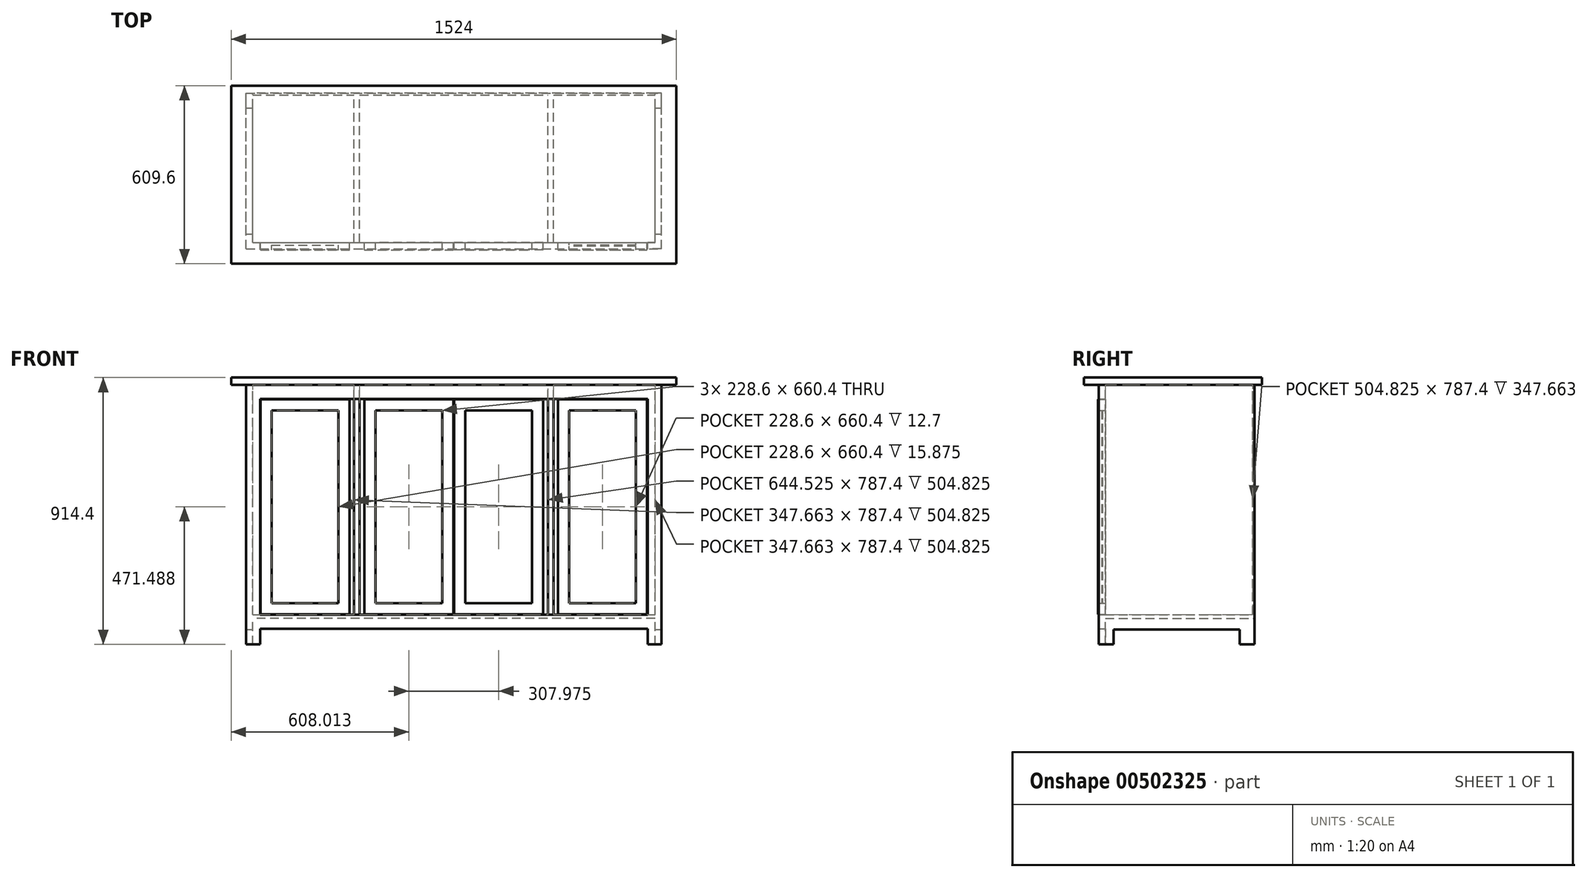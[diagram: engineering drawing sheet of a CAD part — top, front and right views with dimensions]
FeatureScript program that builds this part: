
annotation { "Feature Type Name" : "Feature", "Feature Type Description" : "" }
export const myFeature = defineFeature(function(context is Context, id is Id, definition is map)
    precondition{}
    {
        {
            var Q0;
            Q0=qCreatedBy(makeId("Top.planeOp"),FACE);
            var sketch = newSketch(context, id + "F0", { "sketchPlane" : qUnion([Q0])});
            skLineSegment(sketch, "E0.bottom", {"start": v(762, 304.8) * mm, "end": v(-762, 304.8) * mm});
            skLineSegment(sketch, "E0.top", {"start": v(762, -304.8) * mm, "end": v(-762, -304.8) * mm});
            skLineSegment(sketch, "E0.left", {"start": v(762, 304.8) * mm, "end": v(762, -304.8) * mm});
            skLineSegment(sketch, "E0.right", {"start": v(-762, 304.8) * mm, "end": v(-762, -304.8) * mm});
            skPoint(sketch, "E0.middle", {"position": v(0, 0) * mm});
            skSolve(sketch);
        }
        {
            var Q0;
            Q0=makeQuery(id+"F0.imprint","IMPRINT",FACE,{"disambiguationData":[TD([[makeQuery(id+"F0.imprint","IMPRINT",EDGE,{"derivedFrom":sQuery(id+"F0.wireOp",EDGE,"E0.bottom")}),1.0]])]});
            extrude(context, id + "F1", {"entities" : qUnion([Q0]), "depth" : 25.4 * mm});
        }
        {
            var Q0;
            Q0=makeQuery(id+"F1.opExtrude","CAP_FACE",FACE,{"disambiguationData":[OSD([sQuery(id+"F0.wireOp",EDGE,"E0.bottom"),sQuery(id+"F0.wireOp",EDGE,"E0.top"),sQuery(id+"F0.wireOp",EDGE,"E0.left"),sQuery(id+"F0.wireOp",EDGE,"E0.right")])],"isStart":true});
            var sketch = newSketch(context, id + "F2", { "sketchPlane" : qUnion([Q0])});
            skLineSegment(sketch, "E1.bottom", {"start": v(-711.2, 254) * mm, "end": v(711.2, 254) * mm, "construction": true});
            skLineSegment(sketch, "E1.top", {"start": v(-711.2, -279.4) * mm, "end": v(711.2, -279.4) * mm, "construction": true});
            skLineSegment(sketch, "E1.left", {"start": v(-711.2, 254) * mm, "end": v(-711.2, -279.4) * mm, "construction": true});
            skLineSegment(sketch, "E1.right", {"start": v(711.2, 254) * mm, "end": v(711.2, -279.4) * mm, "construction": true});
            skPoint(sketch, "E1.middle", {"position": v(0, -12.7) * mm});
            skLineSegment(sketch, "E2.bottom", {"start": v(-711.2, 254) * mm, "end": v(-688.98, 254) * mm, "construction": true});
            skLineSegment(sketch, "E2.top", {"start": v(-711.2, 231.78) * mm, "end": v(-688.98, 231.78) * mm, "construction": true});
            skLineSegment(sketch, "E2.left", {"start": v(-711.2, 254) * mm, "end": v(-711.2, 231.78) * mm, "construction": true});
            skLineSegment(sketch, "E2.right", {"start": v(-688.98, 254) * mm, "end": v(-688.98, 231.78) * mm, "construction": true});
            skLineSegment(sketch, "E3.bottom", {"start": v(-711.2, 231.78) * mm, "end": v(-688.98, 231.78) * mm});
            skLineSegment(sketch, "E3.top", {"start": v(-711.2, -279.4) * mm, "end": v(-688.98, -279.4) * mm});
            skLineSegment(sketch, "E3.left", {"start": v(-711.2, 231.78) * mm, "end": v(-711.2, -279.4) * mm});
            skLineSegment(sketch, "E3.right", {"start": v(-688.98, 231.78) * mm, "end": v(-688.98, -279.4) * mm});
            skLineSegment(sketch, "E4.MirrorCS", {"start": v(711.2, 231.78) * mm, "end": v(688.98, 231.78) * mm});
            skLineSegment(sketch, "E5.MirrorCS", {"start": v(711.2, 254) * mm, "end": v(711.2, 231.78) * mm, "construction": true});
            skLineSegment(sketch, "E6.MirrorCS", {"start": v(711.2, 231.78) * mm, "end": v(688.98, 231.78) * mm, "construction": true});
            skLineSegment(sketch, "E7.MirrorCS", {"start": v(688.98, 254) * mm, "end": v(688.98, 231.78) * mm, "construction": true});
            skLineSegment(sketch, "E8.MirrorCS", {"start": v(711.2, 254) * mm, "end": v(688.98, 254) * mm, "construction": true});
            skLineSegment(sketch, "E9.MirrorCS", {"start": v(711.2, -279.4) * mm, "end": v(688.98, -279.4) * mm});
            skLineSegment(sketch, "E10.MirrorCS", {"start": v(711.2, 231.78) * mm, "end": v(711.2, -279.4) * mm});
            skLineSegment(sketch, "E11.MirrorCS", {"start": v(688.98, 231.78) * mm, "end": v(688.98, -279.4) * mm});
            skLineSegment(sketch, "E12", {"start": v(-688.98, 231.78) * mm, "end": v(688.98, 231.78) * mm, "construction": true});
            skLineSegment(sketch, "E13", {"start": v(-688.98, -273.05) * mm, "end": v(688.98, -273.05) * mm, "construction": true});
            skLineSegment(sketch, "E14.bottom", {"start": v(-341.31, 231.78) * mm, "end": v(-322.26, 231.78) * mm});
            skLineSegment(sketch, "E14.top", {"start": v(-341.31, -273.05) * mm, "end": v(-322.26, -273.05) * mm});
            skLineSegment(sketch, "E14.left", {"start": v(-341.31, 231.78) * mm, "end": v(-341.31, -273.05) * mm});
            skLineSegment(sketch, "E14.right", {"start": v(-322.26, 231.77) * mm, "end": v(-322.26, -273.05) * mm});
            skLineSegment(sketch, "E15.MirrorCS", {"start": v(341.31, -273.05) * mm, "end": v(322.26, -273.05) * mm});
            skLineSegment(sketch, "E16.MirrorCS", {"start": v(341.31, 231.78) * mm, "end": v(322.26, 231.78) * mm});
            skLineSegment(sketch, "E17.MirrorCS", {"start": v(322.26, 231.77) * mm, "end": v(322.26, -273.05) * mm});
            skLineSegment(sketch, "E18.MirrorCS", {"start": v(341.31, 231.78) * mm, "end": v(341.31, -273.05) * mm});
            skSolve(sketch);
        }
        {
            var Q0;
            Q0=makeQuery(id+"F2.imprint","IMPRINT",FACE,{"disambiguationData":[TD([[makeQuery(id+"F2.imprint","IMPRINT",EDGE,{"derivedFrom":sQuery(id+"F2.wireOp",EDGE,"E3.bottom")}),-1.0]])]});
            var Q1;
            Q1=makeQuery(id+"F2.imprint","IMPRINT",FACE,{"disambiguationData":[TD([[makeQuery(id+"F2.imprint","IMPRINT",EDGE,{"derivedFrom":sQuery(id+"F2.wireOp",EDGE,"E4.MirrorCS")}),1.0]])]});
            extrude(context, id + "F3", {"entities" : qUnion([Q0, Q1]), "operationType" : NewBodyOperationType.ADD, "depth" : 889 * mm});
        }
        {
            var Q0;
            Q0 = qSketchRegion(id + "F2", true);
            extrude(context, id + "F4", {"entities" : qUnion([Q0]), "operationType" : NewBodyOperationType.ADD, "depth" : 787.4 * mm});
        }
        {
            var Q0;
            Q0=makeQuery(id+"F4.opExtrude","CAP_FACE",FACE,{"disambiguationData":[OSD([sQuery(id+"F2.wireOp",EDGE,"E14.bottom"),sQuery(id+"F2.wireOp",EDGE,"E14.top"),sQuery(id+"F2.wireOp",EDGE,"E14.left"),sQuery(id+"F2.wireOp",EDGE,"E14.right")])],"isStart":false});
            cPlane(context, id + "F5", {"entities" : qUnion([Q0]), "cplaneType" : CPlaneType.OFFSET, "offset" : 0 * mm, "width" : 152.4 * mm, "height" : 152.4 * mm});
        }
        {
            var Q0;
            Q0=qCreatedBy(id+"F5.planeOp",FACE);
            var sketch = newSketch(context, id + "F6", { "sketchPlane" : qUnion([Q0])});
            skLineSegment(sketch, "E19.0", {"start": v(-688.98, 231.78) * mm, "end": v(-688.98, -273.05) * mm});
            skLineSegment(sketch, "E20.0", {"start": v(688.98, 231.78) * mm, "end": v(688.98, -273.05) * mm});
            skLineSegment(sketch, "E21.0", {"start": v(-688.98, -273.05) * mm, "end": v(688.98, -273.05) * mm});
            skLineSegment(sketch, "E22.0", {"start": v(-688.98, 231.78) * mm, "end": v(688.98, 231.78) * mm});
            skPoint(sketch, "E23.orphan", {"position": v(-341.31, 231.78) * mm});
            skPoint(sketch, "E24.orphan", {"position": v(-341.31, -273.05) * mm});
            skPoint(sketch, "E25.orphan", {"position": v(-322.26, -273.05) * mm});
            skPoint(sketch, "E26.orphan", {"position": v(-322.26, 231.78) * mm});
            skPoint(sketch, "E27.orphan", {"position": v(-688.98, -279.4) * mm});
            skPoint(sketch, "E28.orphan", {"position": v(688.98, -279.4) * mm});
            skSolve(sketch);
        }
        {
            var Q0;
            Q0 = qSketchRegion(id + "F6", true);
            extrude(context, id + "F7", {"entities" : qUnion([Q0]), "operationType" : NewBodyOperationType.ADD, "depth" : 12.7 * mm});
        }
        {
            var Q0;
            Q0=makeQuery(id+"F7.boolean.opBoolean","MERGE",FACE,{"derivedFrom":[makeQuery(id+"F4.opExtrude","SWEPT_FACE",FACE,{"disambiguationData":[OSD([sQuery(id+"F2.wireOp",EDGE,"E14.bottom")])]}),makeQuery(id+"F4.opExtrude","SWEPT_FACE",FACE,{"disambiguationData":[OSD([sQuery(id+"F2.wireOp",EDGE,"E16.MirrorCS")])]}),makeQuery(id+"F3.opExtrude","SWEPT_FACE",FACE,{"disambiguationData":[OSD([sQuery(id+"F2.wireOp",EDGE,"E3.bottom")])]}),makeQuery(id+"F3.opExtrude","SWEPT_FACE",FACE,{"disambiguationData":[OSD([sQuery(id+"F2.wireOp",EDGE,"E4.MirrorCS")])]}),makeQuery(id+"F7.opExtrude","SWEPT_FACE",FACE,{"disambiguationData":[OSD([sQuery(id+"F6.wireOp",EDGE,"E22.0")])]})]});
            cPlane(context, id + "F8", {"entities" : qUnion([Q0]), "cplaneType" : CPlaneType.OFFSET, "offset" : 0 * mm, "width" : 152.4 * mm, "height" : 152.4 * mm});
        }
        {
            var Q0;
            Q0=qCreatedBy(id+"F8.planeOp",FACE);
            var sketch = newSketch(context, id + "F9", { "sketchPlane" : qUnion([Q0])});
            skPoint(sketch, "E29.0", {"position": v(-711.2, 0) * mm});
            skPoint(sketch, "E30.0", {"position": v(-688.98, -800.1) * mm});
            skPoint(sketch, "E31.0", {"position": v(688.98, -787.4) * mm});
            skPoint(sketch, "E32.0", {"position": v(688.98, 0) * mm});
            skPoint(sketch, "E33.0", {"position": v(-688.98, -787.4) * mm});
            skLineSegment(sketch, "E34.bottom", {"start": v(-711.2, 0) * mm, "end": v(-663.58, 0) * mm});
            skLineSegment(sketch, "E34.top", {"start": v(-711.2, -889) * mm, "end": v(-663.58, -889) * mm});
            skLineSegment(sketch, "E34.left", {"start": v(-711.2, 0) * mm, "end": v(-711.2, -889) * mm});
            skLineSegment(sketch, "E34.right", {"start": v(-663.58, 0) * mm, "end": v(-663.58, -889) * mm});
            skPoint(sketch, "E35.0", {"position": v(711.2, 0) * mm});
            skLineSegment(sketch, "E36.bottom", {"start": v(711.2, 0) * mm, "end": v(663.58, 0) * mm});
            skLineSegment(sketch, "E36.top", {"start": v(711.2, -889) * mm, "end": v(663.58, -889) * mm});
            skLineSegment(sketch, "E36.left", {"start": v(711.2, 0) * mm, "end": v(711.2, -889) * mm});
            skLineSegment(sketch, "E36.right", {"start": v(663.58, 0) * mm, "end": v(663.58, -889) * mm});
            skLineSegment(sketch, "E37.bottom", {"start": v(-663.58, 0) * mm, "end": v(663.58, 0) * mm});
            skLineSegment(sketch, "E37.top", {"start": v(-663.58, -47.63) * mm, "end": v(663.58, -47.63) * mm});
            skLineSegment(sketch, "E37.left", {"start": v(-663.58, 0) * mm, "end": v(-663.58, -47.63) * mm});
            skLineSegment(sketch, "E37.right", {"start": v(663.58, 0) * mm, "end": v(663.58, -47.63) * mm});
            skLineSegment(sketch, "E38.0", {"start": v(-663.58, -787.4) * mm, "end": v(663.58, -787.4) * mm});
            skPoint(sketch, "E39.orphan", {"position": v(-322.26, -787.4) * mm});
            skPoint(sketch, "E40.orphan", {"position": v(322.26, -787.4) * mm});
            skLineSegment(sketch, "E41", {"start": v(-663.58, -835.03) * mm, "end": v(663.58, -835.03) * mm});
            skLineSegment(sketch, "E42.bottom", {"start": v(-307.98, -787.4) * mm, "end": v(-355.6, -787.4) * mm});
            skLineSegment(sketch, "E42.top", {"start": v(-307.98, -47.63) * mm, "end": v(-355.6, -47.63) * mm});
            skLineSegment(sketch, "E42.left", {"start": v(-307.98, -787.4) * mm, "end": v(-307.97, -47.63) * mm});
            skLineSegment(sketch, "E42.right", {"start": v(-355.6, -787.4) * mm, "end": v(-355.6, -47.63) * mm});
            skPoint(sketch, "E43", {"position": v(-331.79, -787.4) * mm});
            skLineSegment(sketch, "E44", {"start": v(-322.26, -787.4) * mm, "end": v(-341.31, -787.4) * mm, "construction": true});
            skLineSegment(sketch, "E45.MirrorCS", {"start": v(307.98, -787.4) * mm, "end": v(355.6, -787.4) * mm});
            skLineSegment(sketch, "E46.MirrorCS", {"start": v(307.98, -787.4) * mm, "end": v(307.97, -47.63) * mm});
            skLineSegment(sketch, "E47.MirrorCS", {"start": v(355.6, -787.4) * mm, "end": v(355.6, -47.63) * mm});
            skLineSegment(sketch, "E48.MirrorCS", {"start": v(307.98, -47.63) * mm, "end": v(355.6, -47.63) * mm});
            skSolve(sketch);
        }
        {
            var Q0;
            Q0=makeQuery(id+"F9.imprint","IMPRINT",FACE,{"disambiguationData":[TD([[makeQuery(id+"F9.imprint","IMPRINT",EDGE,{"derivedFrom":sQuery(id+"F9.wireOp",EDGE,"E34.bottom")}),-1.0]])]});
            var Q1;
            Q1=makeQuery(id+"F9.imprint","IMPRINT",FACE,{"disambiguationData":[TD([[makeQuery(id+"F9.imprint","IMPRINT",EDGE,{"derivedFrom":sQuery(id+"F9.wireOp",EDGE,"E37.bottom")}),-1.0]])]});
            var Q2;
            {var subQ6=sQuery(id+"F9.wireOp",EDGE,"E41");Q2=makeQuery(id+"F9.imprint","IMPRINT",FACE,{"disambiguationData":[TD([[makeQuery(id+"F9.imprint","IMPRINT",EDGE,{"derivedFrom":subQ6}),1.0]])]});}
            var Q3;
            Q3=makeQuery(id+"F9.imprint","IMPRINT",FACE,{"disambiguationData":[TD([[makeQuery(id+"F9.imprint","IMPRINT",EDGE,{"derivedFrom":sQuery(id+"F9.wireOp",EDGE,"E45.MirrorCS")}),1.0]])]});
            var Q4;
            Q4=makeQuery(id+"F9.imprint","IMPRINT",FACE,{"disambiguationData":[TD([[makeQuery(id+"F9.imprint","IMPRINT",EDGE,{"derivedFrom":sQuery(id+"F9.wireOp",EDGE,"E42.bottom")}),-1.0]])]});
            var Q5;
            Q5=makeQuery(id+"F9.imprint","IMPRINT",FACE,{"disambiguationData":[TD([[makeQuery(id+"F9.imprint","IMPRINT",EDGE,{"derivedFrom":sQuery(id+"F9.wireOp",EDGE,"E36.bottom")}),1.0]])]});
            extrude(context, id + "F10", {"entities" : qUnion([Q0, Q1, Q2, Q3, Q4, Q5]), "operationType" : NewBodyOperationType.ADD, "depth" : 22.22 * mm});
        }
        {
            var Q0;
            Q0=qCreatedBy(id+"F8.planeOp",FACE);
            var sketch = newSketch(context, id + "F11", { "sketchPlane" : qUnion([Q0])});
            skLineSegment(sketch, "E49.bottom", {"start": v(-661.99, -49.21) * mm, "end": v(-623.89, -49.21) * mm});
            skLineSegment(sketch, "E49.top", {"start": v(-661.99, -785.81) * mm, "end": v(-623.89, -785.81) * mm});
            skLineSegment(sketch, "E49.left", {"start": v(-661.99, -49.21) * mm, "end": v(-661.99, -785.81) * mm});
            skLineSegment(sketch, "E49.right", {"start": v(-623.89, -49.21) * mm, "end": v(-623.89, -785.81) * mm});
            skLineSegment(sketch, "E50.bottom", {"start": v(-623.89, -49.21) * mm, "end": v(-395.29, -49.21) * mm});
            skLineSegment(sketch, "E50.top", {"start": v(-623.89, -87.31) * mm, "end": v(-395.29, -87.31) * mm});
            skLineSegment(sketch, "E50.left", {"start": v(-623.89, -49.21) * mm, "end": v(-623.89, -87.31) * mm});
            skLineSegment(sketch, "E50.right", {"start": v(-395.29, -49.21) * mm, "end": v(-395.29, -87.31) * mm});
            skLineSegment(sketch, "E51.bottom", {"start": v(-395.29, -49.21) * mm, "end": v(-357.19, -49.21) * mm});
            skLineSegment(sketch, "E51.top", {"start": v(-395.29, -785.81) * mm, "end": v(-357.19, -785.81) * mm});
            skLineSegment(sketch, "E51.left", {"start": v(-395.29, -49.21) * mm, "end": v(-395.29, -785.81) * mm});
            skLineSegment(sketch, "E51.right", {"start": v(-357.19, -49.21) * mm, "end": v(-357.19, -785.81) * mm});
            skLineSegment(sketch, "E52.bottom", {"start": v(-395.29, -785.81) * mm, "end": v(-623.89, -785.81) * mm});
            skLineSegment(sketch, "E52.top", {"start": v(-395.29, -747.71) * mm, "end": v(-623.89, -747.71) * mm});
            skLineSegment(sketch, "E52.left", {"start": v(-395.29, -785.81) * mm, "end": v(-395.29, -747.71) * mm});
            skLineSegment(sketch, "E52.right", {"start": v(-623.89, -785.81) * mm, "end": v(-623.89, -747.71) * mm});
            skLineSegment(sketch, "E53.MirrorCS", {"start": v(395.29, -785.81) * mm, "end": v(395.29, -747.71) * mm});
            skLineSegment(sketch, "E54.MirrorCS", {"start": v(623.89, -785.81) * mm, "end": v(623.89, -747.71) * mm});
            skLineSegment(sketch, "E55.MirrorCS", {"start": v(661.99, -49.21) * mm, "end": v(623.89, -49.21) * mm});
            skLineSegment(sketch, "E56.MirrorCS", {"start": v(395.29, -785.81) * mm, "end": v(357.19, -785.81) * mm});
            skLineSegment(sketch, "E57.MirrorCS", {"start": v(395.29, -49.21) * mm, "end": v(357.19, -49.21) * mm});
            skLineSegment(sketch, "E58.MirrorCS", {"start": v(661.99, -785.81) * mm, "end": v(623.89, -785.81) * mm});
            skLineSegment(sketch, "E59.MirrorCS", {"start": v(395.29, -49.21) * mm, "end": v(395.29, -87.31) * mm});
            skLineSegment(sketch, "E60.MirrorCS", {"start": v(623.89, -49.21) * mm, "end": v(623.89, -87.31) * mm});
            skLineSegment(sketch, "E61.MirrorCS", {"start": v(395.29, -49.21) * mm, "end": v(395.29, -785.81) * mm});
            skLineSegment(sketch, "E62.MirrorCS", {"start": v(357.19, -49.21) * mm, "end": v(357.19, -785.81) * mm});
            skLineSegment(sketch, "E63.MirrorCS", {"start": v(395.29, -785.81) * mm, "end": v(623.89, -785.81) * mm});
            skLineSegment(sketch, "E64.MirrorCS", {"start": v(395.29, -747.71) * mm, "end": v(623.89, -747.71) * mm});
            skLineSegment(sketch, "E65.MirrorCS", {"start": v(623.89, -49.21) * mm, "end": v(395.29, -49.21) * mm});
            skLineSegment(sketch, "E66.MirrorCS", {"start": v(623.89, -49.21) * mm, "end": v(623.89, -785.81) * mm});
            skLineSegment(sketch, "E67.MirrorCS", {"start": v(623.89, -87.31) * mm, "end": v(395.29, -87.31) * mm});
            skLineSegment(sketch, "E68.MirrorCS", {"start": v(661.99, -49.21) * mm, "end": v(661.99, -785.81) * mm});
            skLineSegment(sketch, "E69.bottom", {"start": v(-306.39, -49.21) * mm, "end": v(-268.29, -49.21) * mm});
            skLineSegment(sketch, "E69.top", {"start": v(-306.39, -785.81) * mm, "end": v(-268.29, -785.81) * mm});
            skLineSegment(sketch, "E69.left", {"start": v(-306.39, -49.21) * mm, "end": v(-306.39, -785.81) * mm});
            skLineSegment(sketch, "E69.right", {"start": v(-268.29, -49.21) * mm, "end": v(-268.29, -785.81) * mm});
            skLineSegment(sketch, "E70.bottom", {"start": v(-268.29, -49.21) * mm, "end": v(-39.69, -49.21) * mm});
            skLineSegment(sketch, "E70.top", {"start": v(-268.29, -87.31) * mm, "end": v(-39.69, -87.31) * mm});
            skLineSegment(sketch, "E70.left", {"start": v(-268.29, -49.21) * mm, "end": v(-268.29, -87.31) * mm});
            skLineSegment(sketch, "E70.right", {"start": v(-39.69, -49.21) * mm, "end": v(-39.69, -87.31) * mm});
            skLineSegment(sketch, "E71.bottom", {"start": v(-39.69, -49.21) * mm, "end": v(-1.59, -49.21) * mm});
            skLineSegment(sketch, "E71.top", {"start": v(-39.69, -785.81) * mm, "end": v(-1.59, -785.81) * mm});
            skLineSegment(sketch, "E71.left", {"start": v(-39.69, -49.21) * mm, "end": v(-39.69, -785.81) * mm});
            skLineSegment(sketch, "E71.right", {"start": v(-1.59, -49.21) * mm, "end": v(-1.59, -785.81) * mm});
            skLineSegment(sketch, "E72.bottom", {"start": v(-39.69, -785.81) * mm, "end": v(-268.29, -785.81) * mm});
            skLineSegment(sketch, "E72.top", {"start": v(-39.69, -747.71) * mm, "end": v(-268.29, -747.71) * mm});
            skLineSegment(sketch, "E72.left", {"start": v(-39.69, -785.81) * mm, "end": v(-39.69, -747.71) * mm});
            skLineSegment(sketch, "E72.right", {"start": v(-268.29, -785.81) * mm, "end": v(-268.29, -747.71) * mm});
            skLineSegment(sketch, "E73.MirrorCS", {"start": v(306.39, -49.21) * mm, "end": v(268.29, -49.21) * mm});
            skLineSegment(sketch, "E74.MirrorCS", {"start": v(39.69, -785.81) * mm, "end": v(1.59, -785.81) * mm});
            skLineSegment(sketch, "E75.MirrorCS", {"start": v(268.29, -785.81) * mm, "end": v(268.29, -747.71) * mm});
            skLineSegment(sketch, "E76.MirrorCS", {"start": v(268.29, -49.21) * mm, "end": v(268.29, -87.31) * mm});
            skLineSegment(sketch, "E77.MirrorCS", {"start": v(39.69, -49.21) * mm, "end": v(1.59, -49.21) * mm});
            skLineSegment(sketch, "E78.MirrorCS", {"start": v(39.69, -785.81) * mm, "end": v(39.69, -747.71) * mm});
            skLineSegment(sketch, "E79.MirrorCS", {"start": v(39.69, -49.21) * mm, "end": v(39.69, -87.31) * mm});
            skLineSegment(sketch, "E80.MirrorCS", {"start": v(306.39, -785.81) * mm, "end": v(268.29, -785.81) * mm});
            skLineSegment(sketch, "E81.MirrorCS", {"start": v(39.69, -747.71) * mm, "end": v(268.29, -747.71) * mm});
            skLineSegment(sketch, "E82.MirrorCS", {"start": v(1.59, -49.21) * mm, "end": v(1.59, -785.81) * mm});
            skLineSegment(sketch, "E83.MirrorCS", {"start": v(39.69, -49.21) * mm, "end": v(39.69, -785.81) * mm});
            skLineSegment(sketch, "E84.MirrorCS", {"start": v(268.29, -49.21) * mm, "end": v(268.29, -785.81) * mm});
            skLineSegment(sketch, "E85.MirrorCS", {"start": v(306.39, -49.21) * mm, "end": v(306.39, -785.81) * mm});
            skLineSegment(sketch, "E86.MirrorCS", {"start": v(268.29, -49.21) * mm, "end": v(39.69, -49.21) * mm});
            skLineSegment(sketch, "E87.MirrorCS", {"start": v(268.29, -87.31) * mm, "end": v(39.69, -87.31) * mm});
            skLineSegment(sketch, "E88.MirrorCS", {"start": v(39.69, -785.81) * mm, "end": v(268.29, -785.81) * mm});
            skSolve(sketch);
        }
        {
            var Q0;
            Q0 = qSketchRegion(id + "F11", true);
            extrude(context, id + "F12", {"entities" : qUnion([Q0]), "depth" : 25.4 * mm});
        }
        {
            var Q0;
            Q0=makeQuery(id+"F1.opExtrude","CAP_FACE",FACE,{"disambiguationData":[OSD([sQuery(id+"F0.wireOp",EDGE,"E0.bottom"),sQuery(id+"F0.wireOp",EDGE,"E0.top"),sQuery(id+"F0.wireOp",EDGE,"E0.left"),sQuery(id+"F0.wireOp",EDGE,"E0.right")])],"isStart":true});
            var sketch = newSketch(context, id + "F13", { "sketchPlane" : qUnion([Q0])});
            skPoint(sketch, "E89.0", {"position": v(-688.98, -279.4) * mm});
            skPoint(sketch, "E90.0", {"position": v(688.98, -273.05) * mm});
            skLineSegment(sketch, "E91.bottom", {"start": v(688.98, -273.05) * mm, "end": v(-688.98, -273.05) * mm});
            skLineSegment(sketch, "E91.top", {"start": v(688.98, -279.4) * mm, "end": v(-688.98, -279.4) * mm});
            skLineSegment(sketch, "E91.left", {"start": v(688.98, -273.05) * mm, "end": v(688.98, -279.4) * mm});
            skLineSegment(sketch, "E91.right", {"start": v(-688.98, -273.05) * mm, "end": v(-688.98, -279.4) * mm});
            skSolve(sketch);
        }
        {
            var Q0;
            Q0 = qSketchRegion(id + "F13", true);
            var Q1;
            Q1=makeQuery(id+"F7.opExtrude","CAP_FACE",FACE,{"disambiguationData":[OSD([sQuery(id+"F6.wireOp",EDGE,"E19.0"),sQuery(id+"F6.wireOp",EDGE,"E20.0"),sQuery(id+"F6.wireOp",EDGE,"E21.0"),sQuery(id+"F6.wireOp",EDGE,"E22.0")])],"isStart":false});
            extrude(context, id + "F14", {"entities" : qUnion([Q0]), "operationType" : NewBodyOperationType.ADD, "endBound" : BoundingType.UP_TO_SURFACE, "endBoundEntityFace" : qUnion([Q1]), "depth" : 25.4 * mm});
        }
        {
            var Q0;
            Q0=makeQuery(id+"F12.opExtrude","SWEPT_FACE",FACE,{"disambiguationData":[OSD([sQuery(id+"F11.wireOp",EDGE,"E52.top")])]});
            var sketch = newSketch(context, id + "F15", { "sketchPlane" : qUnion([Q0])});
            skLineSegment(sketch, "E92.0", {"start": v(-623.89, -257.18) * mm, "end": v(-623.89, -231.78) * mm, "construction": true});
            skLineSegment(sketch, "E93.0", {"start": v(-395.29, -257.18) * mm, "end": v(-395.29, -231.78) * mm, "construction": true});
            skLineSegment(sketch, "E94.bottom", {"start": v(-623.89, -244.48) * mm, "end": v(-395.29, -244.48) * mm});
            skLineSegment(sketch, "E94.top", {"start": v(-623.89, -241.3) * mm, "end": v(-395.29, -241.3) * mm});
            skLineSegment(sketch, "E94.left", {"start": v(-623.89, -244.48) * mm, "end": v(-623.89, -241.3) * mm});
            skLineSegment(sketch, "E94.right", {"start": v(-395.29, -244.48) * mm, "end": v(-395.29, -241.3) * mm});
            skLineSegment(sketch, "E95.MirrorCS", {"start": v(395.29, -244.48) * mm, "end": v(395.29, -241.3) * mm});
            skLineSegment(sketch, "E96.MirrorCS", {"start": v(623.89, -244.48) * mm, "end": v(623.89, -241.3) * mm});
            skLineSegment(sketch, "E97.MirrorCS", {"start": v(623.89, -244.48) * mm, "end": v(395.29, -244.48) * mm});
            skLineSegment(sketch, "E98.MirrorCS", {"start": v(623.89, -241.3) * mm, "end": v(395.29, -241.3) * mm});
            skSolve(sketch);
        }
        {
            var Q0;
            {var subQ0=sQuery(id+"F15.wireOp",EDGE,"E94.top");Q0=makeQuery(id+"F15.imprint","IMPRINT",FACE,{"disambiguationData":[TD([[makeQuery(id+"F15.imprint","IMPRINT",EDGE,{"derivedFrom":subQ0}),1.0]])]});}
            extrude(context, id + "F16", {"entities" : qUnion([Q0]), "operationType" : NewBodyOperationType.ADD, "endBound" : BoundingType.UP_TO_NEXT, "depth" : 25.4 * mm});
        }
        {
            var Q0;
            Q0=makeQuery(id+"F15.imprint","IMPRINT",FACE,{"disambiguationData":[TD([[makeQuery(id+"F15.imprint","IMPRINT",EDGE,{"derivedFrom":sQuery(id+"F15.wireOp",EDGE,"E95.MirrorCS")}),-1.0]])]});
            extrude(context, id + "F17", {"entities" : qUnion([Q0]), "operationType" : NewBodyOperationType.ADD, "endBound" : BoundingType.UP_TO_NEXT, "depth" : 25.4 * mm});
        }
        {
            var Q0;
            Q0=makeQuery(id+"F10.boolean.opBoolean","MERGE",FACE,{"derivedFrom":[makeQuery(id+"F3.opExtrude","SWEPT_FACE",FACE,{"disambiguationData":[OSD([sQuery(id+"F2.wireOp",EDGE,"E10.MirrorCS")])]}),makeQuery(id+"F10.opExtrude","SWEPT_FACE",FACE,{"disambiguationData":[OSD([sQuery(id+"F9.wireOp",EDGE,"E36.left")])]})]});
            var sketch = newSketch(context, id + "F18", { "sketchPlane" : qUnion([Q0])});
            skLineSegment(sketch, "E99.0", {"start": v(-231.78, -800.1) * mm, "end": v(279.4, -800.1) * mm, "construction": true});
            skLineSegment(sketch, "E100.bottom", {"start": v(-203.2, -889) * mm, "end": v(228.6, -889) * mm});
            skLineSegment(sketch, "E100.top", {"start": v(-203.2, -838.2) * mm, "end": v(228.6, -838.2) * mm});
            skLineSegment(sketch, "E100.left", {"start": v(-203.2, -889) * mm, "end": v(-203.2, -889) * mm});
            skLineSegment(sketch, "E100.right", {"start": v(228.6, -889) * mm, "end": v(228.6, -889) * mm});
            skPoint(sketch, "E101.visualSharp", {"position": v(-203.2, -838.2) * mm});
            skArc(sketch, "E101.filletArc", {"start": v(-152.4, -838.2) * mm, "mid": v(-188.32, -853.08) * mm, "end": v(-203.2, -889) * mm, "construction": true});
            skPoint(sketch, "E102.visualSharp", {"position": v(228.6, -838.2) * mm});
            skArc(sketch, "E102.filletArc", {"start": v(228.6, -889) * mm, "mid": v(213.72, -853.08) * mm, "end": v(177.8, -838.2) * mm, "construction": true});
            skLineSegment(sketch, "E103", {"start": v(228.6, -889) * mm, "end": v(228.6, -838.2) * mm});
            skLineSegment(sketch, "E104", {"start": v(-203.2, -889) * mm, "end": v(-203.2, -838.2) * mm});
            skLineSegment(sketch, "E105.0", {"start": v(-231.78, -835.03) * mm, "end": v(-231.78, -889) * mm});
            skLineSegment(sketch, "E106.0", {"start": v(-254, -889) * mm, "end": v(279.4, -889) * mm, "construction": true});
            skSolve(sketch);
        }
        {
            var Q0;
            Q0=makeQuery(id+"F18.imprint","IMPRINT",FACE,{"disambiguationData":[TD([[makeQuery(id+"F18.imprint","IMPRINT",EDGE,{"derivedFrom":sQuery(id+"F18.wireOp",EDGE,"E100.bottom")}),1.0]])]});
            extrude(context, id + "F19", {"entities" : qUnion([Q0]), "operationType" : NewBodyOperationType.REMOVE, "endBound" : BoundingType.THROUGH_ALL, "oppositeDirection" : true, "depth" : 25.4 * mm, "offsetDistance" : 25.4 * mm});
        }
    });
